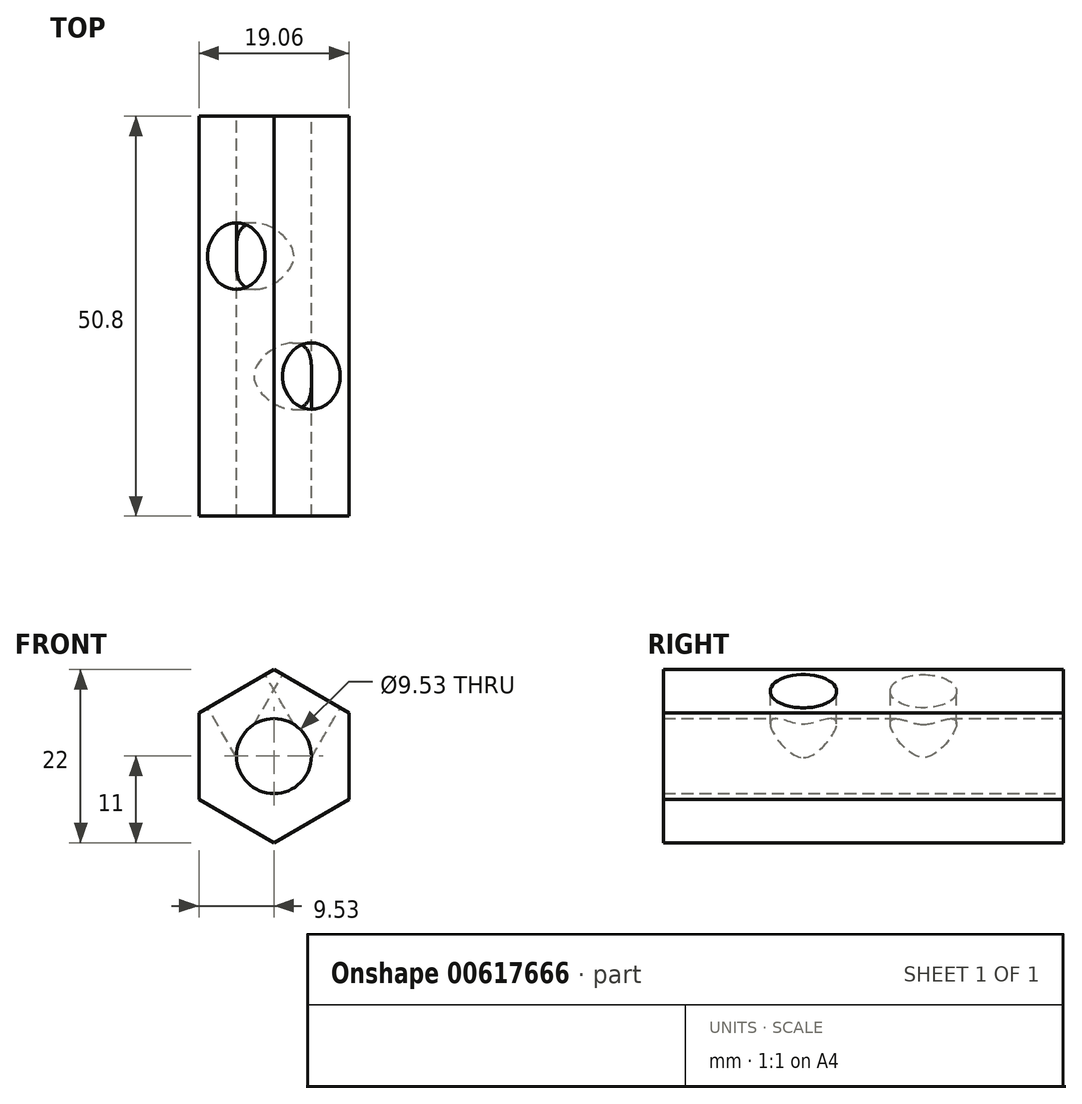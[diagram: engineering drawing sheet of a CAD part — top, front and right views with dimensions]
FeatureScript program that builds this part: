
annotation { "Feature Type Name" : "Feature", "Feature Type Description" : "" }
export const myFeature = defineFeature(function(context is Context, id is Id, definition is map)
    precondition{}
    {
        {
            var Q0;
            Q0=qCreatedBy(makeId("Front.planeOp"),FACE);
            var sketch = newSketch(context, id + "F0", { "sketchPlane" : qUnion([Q0])});
            skCircle(sketch, "E0.cCircle", {"center": v(0, 0) * mm, "radius": 9.53 * mm, "construction": true});
            skLineSegment(sketch, "E0.0", {"start": v(0, 11) * mm, "end": v(9.53, 5.5) * mm});
            skLineSegment(sketch, "E0.1", {"start": v(9.53, 5.5) * mm, "end": v(9.53, -5.5) * mm});
            skLineSegment(sketch, "E0.2", {"start": v(9.52, -5.5) * mm, "end": v(0, -11) * mm});
            skLineSegment(sketch, "E0.3", {"start": v(0, -11) * mm, "end": v(-9.52, -5.5) * mm});
            skLineSegment(sketch, "E0.4", {"start": v(-9.53, -5.5) * mm, "end": v(-9.52, 5.5) * mm});
            skLineSegment(sketch, "E0.5", {"start": v(-9.52, 5.5) * mm, "end": v(0, 11) * mm});
            skPoint(sketch, "E0.0.midPoint", {"position": v(4.76, 8.25) * mm});
            skCircle(sketch, "E1", {"center": v(0, 0) * mm, "radius": 4.76 * mm});
            skSolve(sketch);
        }
        {
            var Q0;
            Q0=makeQuery(id+"F0.imprint","IMPRINT",FACE,{"disambiguationData":[TD([[makeQuery(id+"F0.imprint","IMPRINT",EDGE,{"derivedFrom":sQuery(id+"F0.wireOp",EDGE,"E0.0")}),-1.0]])]});
            extrude(context, id + "F1", {"entities" : qUnion([Q0]), "depth" : 50.8 * mm, "offsetDistance" : 25.4 * mm});
        }
        {
            var Q0;
            Q0=makeQuery(id+"F1.opExtrude","SWEPT_FACE",FACE,{"disambiguationData":[OSD([sQuery(id+"F0.wireOp",EDGE,"E0.0")])]});
            var sketch = newSketch(context, id + "F2", { "sketchPlane" : qUnion([Q0])});
            skPoint(sketch, "E2", {"position": v(0, -62.83) * mm});
            skPoint(sketch, "E3", {"position": v(0, -33.02) * mm});
            skSolve(sketch);
        }
        {
            var Q0;
            Q0=sQuery(id+"F2.wireOp",VERTEX,"E3");
            var Q1;
            Q1=sQuery(id+"F2.wireOp",VERTEX,"63302b6f-bd60-43f1-b8db-b52b097adef4");
            var Q2;
            Q2=makeQuery(id+"F1.opExtrude","SWEPT_BODY",BODY,{"disambiguationData":[OSD([sQuery(id+"F0.wireOp",EDGE,"E0.0"),sQuery(id+"F0.wireOp",EDGE,"E0.1"),sQuery(id+"F0.wireOp",EDGE,"E0.2"),sQuery(id+"F0.wireOp",EDGE,"E0.3"),sQuery(id+"F0.wireOp",EDGE,"E0.4"),sQuery(id+"F0.wireOp",EDGE,"E0.5"),sQuery(id+"F0.wireOp",EDGE,"E1")])]});
            hole(context, id + "F3", {"style" : HoleStyle.SIMPLE, "endStyle" : HoleEndStyle.BLIND, "holeDiameter" : 8.43 * mm, "majorDiameter" : 6.35 * mm, "holeDepth" : 8.9 * mm, "isTappedThrough" : true, "tappedDepth" : 12.7 * mm, "tapClearance" : 3, "locations" : qUnion([Q0, Q1]), "scope" : qUnion([Q2])});
        }
        {
            var Q0;
            Q0=qCreatedBy(makeId("Right.planeOp"),FACE);
            var sketch = newSketch(context, id + "F4", { "sketchPlane" : qUnion([Q0])});
            skPoint(sketch, "E4.0", {"position": v(-50.8, 0) * mm});
            skLineSegment(sketch, "E5", {"start": v(-50.8, 0) * mm, "end": v(0, 0) * mm});
            skSolve(sketch);
        }
        {
            var Q0;
            Q0=makeQuery(id+"F1.opExtrude","SWEPT_FACE",FACE,{"disambiguationData":[OSD([sQuery(id+"F0.wireOp",EDGE,"E0.5")])]});
            var sketch = newSketch(context, id + "F5", { "sketchPlane" : qUnion([Q0])});
            skPoint(sketch, "E6", {"position": v(0, -17.78) * mm});
            skSolve(sketch);
        }
        {
            var Q0;
            Q0=qCreatedBy(makeId("Top.planeOp"),FACE);
            var sketch = newSketch(context, id + "F6", { "sketchPlane" : qUnion([Q0])});
            skPoint(sketch, "E7.0", {"position": v(0, -50.8) * mm});
            skLineSegment(sketch, "E8", {"start": v(0, 0) * mm, "end": v(0, -50.8) * mm});
            skSolve(sketch);
        }
        {
            var Q0;
            Q0=sQuery(id+"F5.wireOp",VERTEX,"E6");
            var Q1;
            Q1=makeQuery(id+"F1.opExtrude","SWEPT_BODY",BODY,{"disambiguationData":[OSD([sQuery(id+"F0.wireOp",EDGE,"E0.0"),sQuery(id+"F0.wireOp",EDGE,"E0.1"),sQuery(id+"F0.wireOp",EDGE,"E0.2"),sQuery(id+"F0.wireOp",EDGE,"E0.3"),sQuery(id+"F0.wireOp",EDGE,"E0.4"),sQuery(id+"F0.wireOp",EDGE,"E0.5"),sQuery(id+"F0.wireOp",EDGE,"E1")])]});
            hole(context, id + "F7", {"style" : HoleStyle.SIMPLE, "endStyle" : HoleEndStyle.BLIND, "holeDiameter" : 8.43 * mm, "majorDiameter" : 6.35 * mm, "holeDepth" : 10.16 * mm, "isTappedThrough" : true, "tappedDepth" : 12.7 * mm, "tapClearance" : 3, "startFromSketch" : true, "locations" : qUnion([Q0]), "scope" : qUnion([Q1])});
        }
    });
